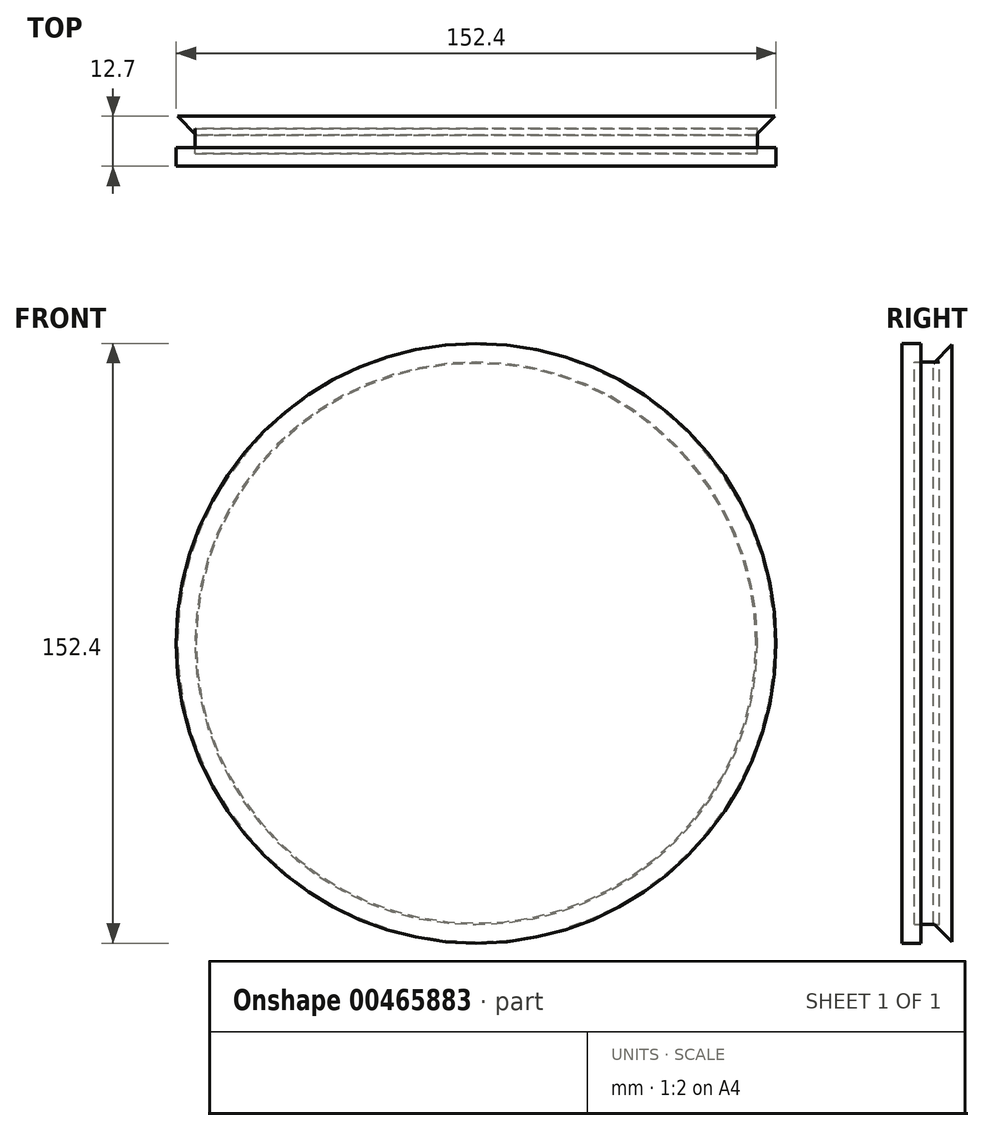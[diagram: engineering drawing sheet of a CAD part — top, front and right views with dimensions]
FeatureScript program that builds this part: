
annotation { "Feature Type Name" : "Feature", "Feature Type Description" : "" }
export const myFeature = defineFeature(function(context is Context, id is Id, definition is map)
    precondition{}
    {
        {
            var Q0;
            Q0=qCreatedBy(makeId("Front.planeOp"),FACE);
            var sketch = newSketch(context, id + "F0", { "sketchPlane" : qUnion([Q0])});
            skCircle(sketch, "E0", {"center": v(0, 0) * mm, "radius": 76.2 * mm});
            skSolve(sketch);
        }
        {
            var Q0;
            Q0=makeQuery(id+"F0.imprint","IMPRINT",FACE,{"disambiguationData":[TD([[makeQuery(id+"F0.imprint","IMPRINT",EDGE,{"derivedFrom":sQuery(id+"F0.wireOp",EDGE,"E0")}),1.0]])]});
            extrude(context, id + "F1", {"entities" : qUnion([Q0]), "endBound" : BoundingType.SYMMETRIC, "depth" : 12.7 * mm, "offsetDistance" : 25.4 * mm});
        }
        {
            var Q0;
            Q0=qCreatedBy(makeId("Front.planeOp"),FACE);
            var sketch = newSketch(context, id + "F2", { "sketchPlane" : qUnion([Q0])});
            skCircle(sketch, "E1", {"center": v(0, 0) * mm, "radius": 76.2 * mm});
            skSolve(sketch);
        }
        {
            var Q0;
            Q0 = qSketchRegion(id + "F2", true);
            extrude(context, id + "F3", {"entities" : qUnion([Q0]), "operationType" : NewBodyOperationType.REMOVE, "endBound" : BoundingType.SYMMETRIC, "depth" : 3.17 * mm, "offsetDistance" : 25.4 * mm});
        }
        {
            var Q0;
            Q0=qCreatedBy(makeId("Front.planeOp"),FACE);
            var sketch = newSketch(context, id + "F4", { "sketchPlane" : qUnion([Q0])});
            skCircle(sketch, "E2", {"center": v(0, 0) * mm, "radius": 71.44 * mm});
            skSolve(sketch);
        }
        {
            var Q0;
            Q0 = qSketchRegion(id + "F4", true);
            extrude(context, id + "F5", {"entities" : qUnion([Q0]), "endBound" : BoundingType.SYMMETRIC, "depth" : 6.35 * mm, "offsetDistance" : 25.4 * mm});
        }
        {
            var Q0;
            Q0=makeQuery(id+"F3.boolean.opBoolean","COPY",EDGE,{"derivedFrom":makeQuery(id+"F3.opExtrude","CAP_EDGE",EDGE,{"disambiguationData":[OSD([sQuery(id+"F2.wireOp",EDGE,"E1")])],"isStart":false})});
            var Q1;
            Q1=makeQuery(id+"F3.boolean.opBoolean","COPY",EDGE,{"derivedFrom":makeQuery(id+"F3.opExtrude","CAP_EDGE",EDGE,{"disambiguationData":[OSD([sQuery(id+"F2.wireOp",EDGE,"E1")])],"isStart":true})});
            chamfer(context, id + "F6", {"entities" : qUnion([Q0, Q1]), "width" : 5.08 * mm, "tangentPropagation" : true});
        }
    });
